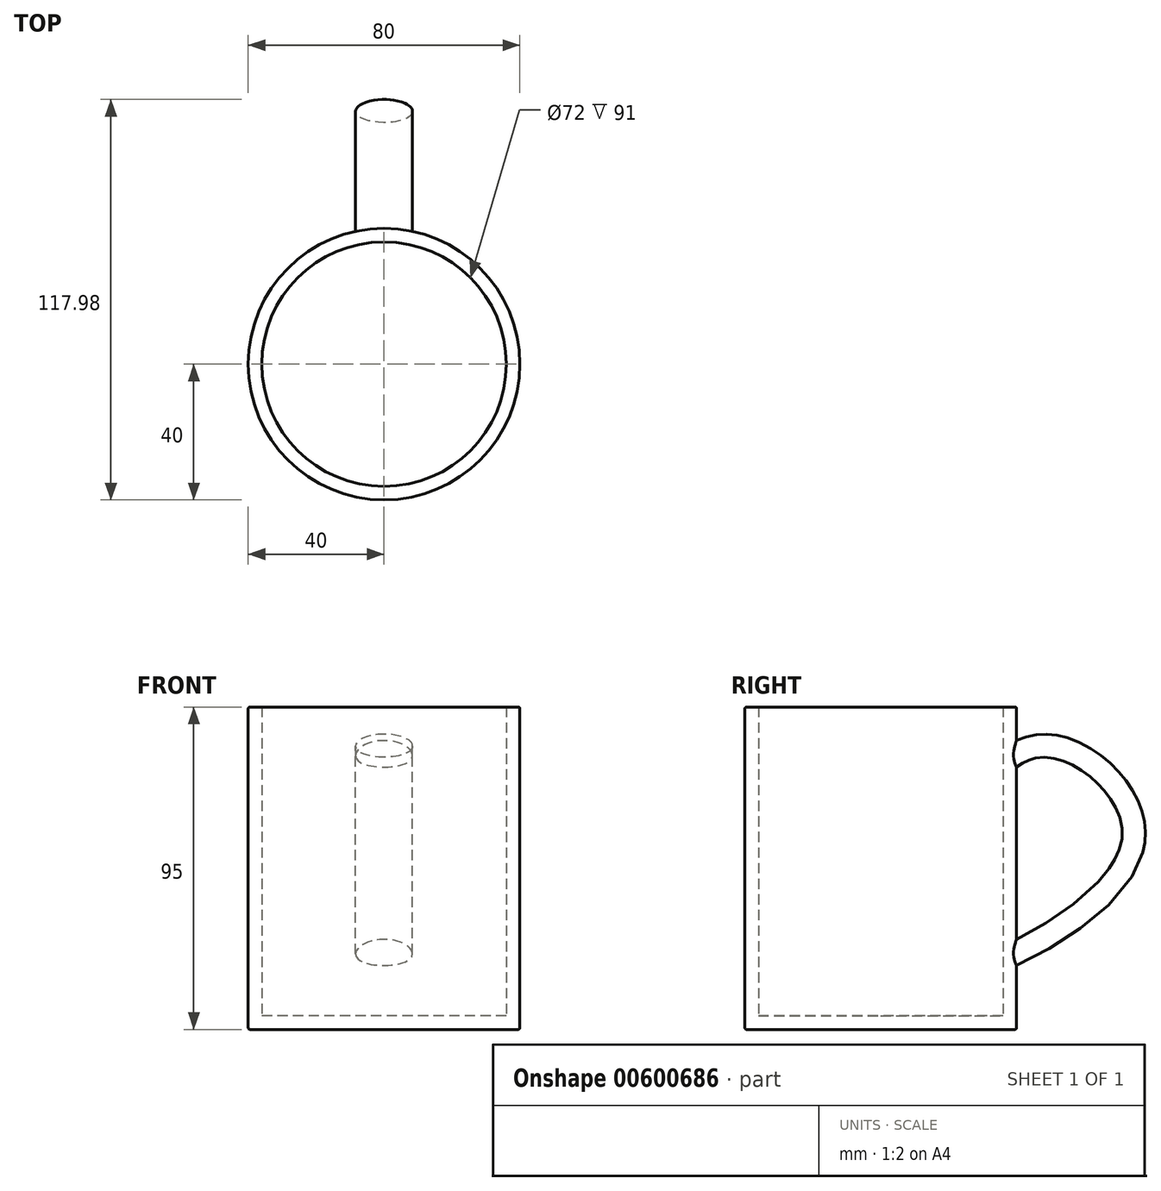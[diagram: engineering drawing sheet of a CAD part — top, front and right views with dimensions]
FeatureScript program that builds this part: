
annotation { "Feature Type Name" : "Feature", "Feature Type Description" : "" }
export const myFeature = defineFeature(function(context is Context, id is Id, definition is map)
    precondition{}
    {
        {
            var Q0;
            Q0=qCreatedBy(makeId("Top.planeOp"),FACE);
            var sketch = newSketch(context, id + "F0", { "sketchPlane" : qUnion([Q0])});
            skCircle(sketch, "E0", {"center": v(0, 0) * mm, "radius": 40 * mm});
            skSolve(sketch);
        }
        {
            var Q0;
            Q0 = qSketchRegion(id + "F0", true);
            extrude(context, id + "F1", {"entities" : qUnion([Q0]), "depth" : 95 * mm, "offsetDistance" : 25 * mm});
        }
        {
            var Q0;
            Q0=qCreatedBy(makeId("Right.planeOp"),FACE);
            var sketch = newSketch(context, id + "F2", { "sketchPlane" : qUnion([Q0])});
            skFitSpline(sketch, "E1", {"points": [v(17.51, 62) * mm, v(47.92, 84.38) * mm, v(75.36, 57.55) * mm, v(24.86, 15.42) * mm], "startDerivative": vector(89.92, 77.72) * mm, "endDerivative": vector(-177, -61.82) * mm});
            skSolve(sketch);
        }
        {
            var Q0;
            Q0=qCreatedBy(makeId("Front.planeOp"),FACE);
            cPlane(context, id + "F3", {"entities" : qUnion([Q0]), "cplaneType" : CPlaneType.OFFSET, "offset" : 40 * mm, "oppositeDirection" : true, "width" : 150 * mm, "height" : 150 * mm});
        }
        {
            var Q0;
            Q0=qCreatedBy(id+"F3.planeOp",FACE);
            var sketch = newSketch(context, id + "F4", { "sketchPlane" : qUnion([Q0])});
            skEllipse(sketch, "E2", {"center": v(0, 81.21) * mm, "majorRadius": 8.39 * mm, "minorRadius": 3.9 * mm, "majorAxis": v(-1, 0)});
            skSolve(sketch);
        }
        {
            var Q0;
            Q0=makeQuery(id+"F4.imprint","IMPRINT",FACE,{"disambiguationData":[TD([[makeQuery(id+"F4.imprint","IMPRINT",EDGE,{"derivedFrom":sQuery(id+"F4.wireOp",EDGE,"E2")}),1.0]])]});
            var Q1;
            Q1=sQuery(id+"F2.wireOp",EDGE,"E1");
            sweep(context, id + "F5", {"operationType" : NewBodyOperationType.ADD, "profiles" : qUnion([Q0]), "path" : qUnion([Q1])});
        }
        {
            var Q0;
            Q0=makeQuery(id+"F1.opExtrude","CAP_FACE",FACE,{"disambiguationData":[OSD([sQuery(id+"F0.wireOp",EDGE,"E0")])],"isStart":false});
            shell(context, id + "F6", {"entities" : qUnion([Q0]), "thickness" : 4 * mm});
        }
        {
            var Q0;
            Q0=makeQuery(id+"F1.opExtrude","CAP_EDGE",EDGE,{"disambiguationData":[OSD([sQuery(id+"F0.wireOp",EDGE,"E0")])],"isStart":false});
            var Q1;
            Q1=makeQuery(id+"F1.opExtrude","CAP_EDGE",EDGE,{"disambiguationData":[OSD([sQuery(id+"F0.wireOp",EDGE,"E0")])],"isStart":true});
            fillet(context, id + "F7", {"entities" : qUnion([Q0, Q1]), "radius" : 0.5 * mm, "tangentPropagation" : true, "allowEdgeOverflow" : false});
        }
    });
